annotation { "Feature Type Name" : "Feature", "Feature Type Description" : "" }
export const myFeature = defineFeature(function(context is Context, id is Id, definition is map)
    precondition{}
    {
        {
            var Q0;
            Q0=qCreatedBy(makeId("Front.planeOp"),FACE);
            var sketch = newSketch(context, id + "F0", { "sketchPlane" : qUnion([Q0])});
            skCircle(sketch, "E0", {"center": v(0, 0) * mm, "radius": 38.1 * mm});
            skCircle(sketch, "E1", {"center": v(0, 0) * mm, "radius": 50.8 * mm});
            skLineSegment(sketch, "E2", {"start": v(0, 46.58) * mm, "end": v(0, 31.75) * mm});
            skLineSegment(sketch, "E3", {"start": v(0, 63.5) * mm, "end": v(0, 50.8) * mm});
            skLineSegment(sketch, "E4.1.0", {"start": v(-27.38, 37.68) * mm, "end": v(-18.66, 25.69) * mm});
            skLineSegment(sketch, "E4.2.0", {"start": v(-44.3, 14.4) * mm, "end": v(-30.2, 9.81) * mm});
            skLineSegment(sketch, "E4.3.0", {"start": v(-44.3, -14.4) * mm, "end": v(-30.2, -9.81) * mm});
            skLineSegment(sketch, "E4.4.0", {"start": v(-27.38, -37.68) * mm, "end": v(-18.66, -25.69) * mm});
            skLineSegment(sketch, "E4.6.0", {"start": v(27.38, -37.68) * mm, "end": v(18.66, -25.69) * mm});
            skLineSegment(sketch, "E4.7.0", {"start": v(44.3, -14.4) * mm, "end": v(30.2, -9.81) * mm});
            skLineSegment(sketch, "E4.8.0", {"start": v(44.3, 14.4) * mm, "end": v(30.2, 9.81) * mm});
            skLineSegment(sketch, "E4.9.0", {"start": v(27.38, 37.68) * mm, "end": v(18.66, 25.69) * mm});
            skLineSegment(sketch, "E5.1.0", {"start": v(-28.57, 49.5) * mm, "end": v(-25.4, 44) * mm});
            skLineSegment(sketch, "E5.2.0", {"start": v(-49.5, 28.58) * mm, "end": v(-44, 25.4) * mm});
            skLineSegment(sketch, "E5.3.0", {"start": v(-63.5, 0) * mm, "end": v(-50.8, 0) * mm});
            skLineSegment(sketch, "E5.4.0", {"start": v(-49.5, -28.57) * mm, "end": v(-44, -25.4) * mm});
            skLineSegment(sketch, "E5.5.0", {"start": v(-28.57, -49.5) * mm, "end": v(-25.4, -44) * mm});
            skLineSegment(sketch, "E5.6.0", {"start": v(0, -63.5) * mm, "end": v(0, -50.8) * mm});
            skLineSegment(sketch, "E5.7.0", {"start": v(28.57, -49.5) * mm, "end": v(25.4, -44) * mm});
            skLineSegment(sketch, "E5.8.0", {"start": v(49.5, -28.58) * mm, "end": v(44, -25.4) * mm});
            skLineSegment(sketch, "E5.9.0", {"start": v(63.5, 0) * mm, "end": v(50.8, 0) * mm});
            skLineSegment(sketch, "E5.10.0", {"start": v(49.5, 28.58) * mm, "end": v(44, 25.4) * mm});
            skLineSegment(sketch, "E5.11.0", {"start": v(28.58, 49.5) * mm, "end": v(25.4, 44) * mm});
            skCircle(sketch, "E6.0", {"center": v(0, 0) * mm, "radius": 31.75 * mm});
            skPoint(sketch, "E7.orphan", {"position": v(0, 57.15) * mm});
            skPoint(sketch, "E8.orphan", {"position": v(57.15, 0) * mm});
            skPoint(sketch, "E9.orphan", {"position": v(0, -57.15) * mm});
            skPoint(sketch, "E10.orphan", {"position": v(-57.15, 0) * mm});
            skPoint(sketch, "E11.orphan", {"position": v(0, 38.1) * mm});
            skPoint(sketch, "E12.orphan", {"position": v(22.4, 30.82) * mm});
            skPoint(sketch, "E13.orphan", {"position": v(36.24, 11.77) * mm});
            skPoint(sketch, "E14.orphan", {"position": v(36.24, -11.77) * mm});
            skPoint(sketch, "E15.orphan", {"position": v(22.4, -30.82) * mm});
            skPoint(sketch, "E16.orphan", {"position": v(0, -38.1) * mm});
            skPoint(sketch, "E17.orphan", {"position": v(-22.4, -30.82) * mm});
            skPoint(sketch, "E18.orphan", {"position": v(-36.24, -11.77) * mm});
            skPoint(sketch, "E19.orphan", {"position": v(-36.24, 11.77) * mm});
            skPoint(sketch, "E20.orphan", {"position": v(-22.4, 30.82) * mm});
            skCircle(sketch, "E21.0", {"center": v(0, 0) * mm, "radius": 53.98 * mm});
            skLineSegment(sketch, "E22", {"start": v(0, 50.8) * mm, "end": v(0, 53.98) * mm});
            skLineSegment(sketch, "E23", {"start": v(0, -50.8) * mm, "end": v(0, -53.98) * mm});
            skLineSegment(sketch, "E24.1.0", {"start": v(5.31, -50.52) * mm, "end": v(5.64, -53.68) * mm});
            skLineSegment(sketch, "E24.2.0", {"start": v(10.56, -49.69) * mm, "end": v(11.22, -52.8) * mm});
            skLineSegment(sketch, "E24.3.0", {"start": v(15.7, -48.31) * mm, "end": v(16.68, -51.33) * mm});
            skLineSegment(sketch, "E24.4.0", {"start": v(20.66, -46.4) * mm, "end": v(21.95, -49.3) * mm});
            skLineSegment(sketch, "E24.5.0", {"start": v(25.4, -44) * mm, "end": v(26.99, -46.74) * mm});
            skLineSegment(sketch, "E24.6.0", {"start": v(29.86, -41.1) * mm, "end": v(31.73, -43.67) * mm});
            skLineSegment(sketch, "E24.7.0", {"start": v(34, -37.75) * mm, "end": v(36.12, -40.11) * mm});
            skLineSegment(sketch, "E24.8.0", {"start": v(37.75, -34) * mm, "end": v(40.11, -36.12) * mm});
            skLineSegment(sketch, "E24.9.0", {"start": v(41.1, -29.86) * mm, "end": v(43.67, -31.73) * mm});
            skLineSegment(sketch, "E24.10.0", {"start": v(44, -25.4) * mm, "end": v(46.74, -26.99) * mm});
            skLineSegment(sketch, "E24.11.0", {"start": v(46.4, -20.66) * mm, "end": v(49.3, -21.95) * mm});
            skLineSegment(sketch, "E24.12.0", {"start": v(48.31, -15.7) * mm, "end": v(51.33, -16.68) * mm});
            skLineSegment(sketch, "E24.13.0", {"start": v(49.69, -10.56) * mm, "end": v(52.8, -11.22) * mm});
            skLineSegment(sketch, "E24.14.0", {"start": v(50.52, -5.31) * mm, "end": v(53.68, -5.64) * mm});
            skLineSegment(sketch, "E24.15.0", {"start": v(50.8, 0) * mm, "end": v(53.98, 0) * mm});
            skLineSegment(sketch, "E24.16.0", {"start": v(50.52, 5.31) * mm, "end": v(53.68, 5.64) * mm});
            skLineSegment(sketch, "E24.17.0", {"start": v(49.69, 10.56) * mm, "end": v(52.8, 11.22) * mm});
            skLineSegment(sketch, "E24.18.0", {"start": v(48.31, 15.7) * mm, "end": v(51.33, 16.68) * mm});
            skLineSegment(sketch, "E24.19.0", {"start": v(46.4, 20.66) * mm, "end": v(49.3, 21.95) * mm});
            skLineSegment(sketch, "E24.20.0", {"start": v(44, 25.4) * mm, "end": v(46.74, 26.99) * mm});
            skLineSegment(sketch, "E24.21.0", {"start": v(41.1, 29.86) * mm, "end": v(43.67, 31.73) * mm});
            skLineSegment(sketch, "E24.22.0", {"start": v(37.75, 34) * mm, "end": v(40.11, 36.12) * mm});
            skLineSegment(sketch, "E24.23.0", {"start": v(34, 37.75) * mm, "end": v(36.12, 40.11) * mm});
            skLineSegment(sketch, "E24.24.0", {"start": v(29.86, 41.1) * mm, "end": v(31.73, 43.67) * mm});
            skLineSegment(sketch, "E24.25.0", {"start": v(25.4, 44) * mm, "end": v(26.99, 46.74) * mm});
            skLineSegment(sketch, "E24.26.0", {"start": v(20.66, 46.4) * mm, "end": v(21.95, 49.3) * mm});
            skLineSegment(sketch, "E24.27.0", {"start": v(15.7, 48.31) * mm, "end": v(16.68, 51.33) * mm});
            skLineSegment(sketch, "E24.28.0", {"start": v(10.56, 49.69) * mm, "end": v(11.22, 52.8) * mm});
            skLineSegment(sketch, "E24.29.0", {"start": v(5.31, 50.52) * mm, "end": v(5.64, 53.68) * mm});
            skLineSegment(sketch, "E24.31.0", {"start": v(-5.31, 50.52) * mm, "end": v(-5.64, 53.68) * mm});
            skLineSegment(sketch, "E24.32.0", {"start": v(-10.56, 49.69) * mm, "end": v(-11.22, 52.8) * mm});
            skLineSegment(sketch, "E24.33.0", {"start": v(-15.7, 48.31) * mm, "end": v(-16.68, 51.33) * mm});
            skLineSegment(sketch, "E24.34.0", {"start": v(-20.66, 46.4) * mm, "end": v(-21.95, 49.3) * mm});
            skLineSegment(sketch, "E24.35.0", {"start": v(-25.4, 44) * mm, "end": v(-26.99, 46.74) * mm});
            skLineSegment(sketch, "E24.36.0", {"start": v(-29.86, 41.1) * mm, "end": v(-31.73, 43.67) * mm});
            skLineSegment(sketch, "E24.37.0", {"start": v(-34, 37.75) * mm, "end": v(-36.12, 40.11) * mm});
            skLineSegment(sketch, "E24.38.0", {"start": v(-37.75, 34) * mm, "end": v(-40.11, 36.12) * mm});
            skLineSegment(sketch, "E24.39.0", {"start": v(-41.1, 29.86) * mm, "end": v(-43.67, 31.73) * mm});
            skLineSegment(sketch, "E24.40.0", {"start": v(-44, 25.4) * mm, "end": v(-46.74, 26.99) * mm});
            skLineSegment(sketch, "E24.41.0", {"start": v(-46.4, 20.66) * mm, "end": v(-49.3, 21.95) * mm});
            skLineSegment(sketch, "E24.42.0", {"start": v(-48.31, 15.7) * mm, "end": v(-51.33, 16.68) * mm});
            skLineSegment(sketch, "E24.43.0", {"start": v(-49.69, 10.56) * mm, "end": v(-52.8, 11.22) * mm});
            skLineSegment(sketch, "E24.44.0", {"start": v(-50.52, 5.31) * mm, "end": v(-53.68, 5.64) * mm});
            skLineSegment(sketch, "E24.45.0", {"start": v(-50.8, 0) * mm, "end": v(-53.98, 0) * mm});
            skLineSegment(sketch, "E24.46.0", {"start": v(-50.52, -5.31) * mm, "end": v(-53.68, -5.64) * mm});
            skLineSegment(sketch, "E24.47.0", {"start": v(-49.69, -10.56) * mm, "end": v(-52.8, -11.22) * mm});
            skLineSegment(sketch, "E24.48.0", {"start": v(-48.31, -15.7) * mm, "end": v(-51.33, -16.68) * mm});
            skLineSegment(sketch, "E24.49.0", {"start": v(-46.4, -20.66) * mm, "end": v(-49.3, -21.95) * mm});
            skLineSegment(sketch, "E24.50.0", {"start": v(-44, -25.4) * mm, "end": v(-46.74, -26.99) * mm});
            skLineSegment(sketch, "E24.51.0", {"start": v(-41.1, -29.86) * mm, "end": v(-43.67, -31.73) * mm});
            skLineSegment(sketch, "E24.52.0", {"start": v(-37.75, -34) * mm, "end": v(-40.11, -36.12) * mm});
            skLineSegment(sketch, "E24.53.0", {"start": v(-34, -37.75) * mm, "end": v(-36.12, -40.11) * mm});
            skLineSegment(sketch, "E24.54.0", {"start": v(-29.86, -41.1) * mm, "end": v(-31.73, -43.67) * mm});
            skLineSegment(sketch, "E24.55.0", {"start": v(-25.4, -44) * mm, "end": v(-26.99, -46.74) * mm});
            skLineSegment(sketch, "E24.56.0", {"start": v(-20.66, -46.4) * mm, "end": v(-21.95, -49.3) * mm});
            skLineSegment(sketch, "E24.57.0", {"start": v(-15.7, -48.31) * mm, "end": v(-16.68, -51.33) * mm});
            skLineSegment(sketch, "E24.58.0", {"start": v(-10.56, -49.69) * mm, "end": v(-11.22, -52.8) * mm});
            skLineSegment(sketch, "E24.59.0", {"start": v(-5.31, -50.52) * mm, "end": v(-5.64, -53.68) * mm});
            skLineSegment(sketch, "E25", {"start": v(0, -31.75) * mm, "end": v(0, -38.1) * mm});
            skLineSegment(sketch, "E26.1.0", {"start": v(2, -31.69) * mm, "end": v(2.4, -38.02) * mm});
            skLineSegment(sketch, "E26.2.0", {"start": v(3.98, -31.5) * mm, "end": v(4.78, -37.8) * mm});
            skLineSegment(sketch, "E26.3.0", {"start": v(5.95, -31.19) * mm, "end": v(7.14, -37.43) * mm});
            skLineSegment(sketch, "E26.4.0", {"start": v(7.9, -30.75) * mm, "end": v(9.48, -36.9) * mm});
            skLineSegment(sketch, "E26.5.0", {"start": v(9.81, -30.2) * mm, "end": v(11.77, -36.24) * mm});
            skLineSegment(sketch, "E26.6.0", {"start": v(11.69, -29.52) * mm, "end": v(14.03, -35.42) * mm});
            skLineSegment(sketch, "E26.7.0", {"start": v(13.52, -28.73) * mm, "end": v(16.22, -34.47) * mm});
            skLineSegment(sketch, "E26.8.0", {"start": v(15.3, -27.82) * mm, "end": v(18.35, -33.39) * mm});
            skLineSegment(sketch, "E26.9.0", {"start": v(17.01, -26.8) * mm, "end": v(20.41, -32.17) * mm});
            skLineSegment(sketch, "E26.10.0", {"start": v(18.66, -25.69) * mm, "end": v(22.4, -30.82) * mm});
            skLineSegment(sketch, "E26.11.0", {"start": v(20.24, -24.46) * mm, "end": v(24.29, -29.36) * mm});
            skLineSegment(sketch, "E26.12.0", {"start": v(21.73, -23.14) * mm, "end": v(26.08, -27.77) * mm});
            skLineSegment(sketch, "E26.13.0", {"start": v(23.14, -21.73) * mm, "end": v(27.77, -26.08) * mm});
            skLineSegment(sketch, "E26.14.0", {"start": v(24.46, -20.24) * mm, "end": v(29.36, -24.29) * mm});
            skLineSegment(sketch, "E26.15.0", {"start": v(25.69, -18.66) * mm, "end": v(30.82, -22.4) * mm});
            skLineSegment(sketch, "E26.16.0", {"start": v(26.8, -17.01) * mm, "end": v(32.17, -20.42) * mm});
            skLineSegment(sketch, "E26.17.0", {"start": v(27.82, -15.3) * mm, "end": v(33.39, -18.35) * mm});
            skLineSegment(sketch, "E26.18.0", {"start": v(28.73, -13.52) * mm, "end": v(34.47, -16.22) * mm});
            skLineSegment(sketch, "E26.19.0", {"start": v(29.52, -11.69) * mm, "end": v(35.42, -14.03) * mm});
            skLineSegment(sketch, "E26.20.0", {"start": v(30.2, -9.81) * mm, "end": v(36.24, -11.77) * mm});
            skLineSegment(sketch, "E26.21.0", {"start": v(30.75, -7.9) * mm, "end": v(36.9, -9.48) * mm});
            skLineSegment(sketch, "E26.22.0", {"start": v(31.19, -5.95) * mm, "end": v(37.43, -7.14) * mm});
            skLineSegment(sketch, "E26.23.0", {"start": v(31.5, -3.98) * mm, "end": v(37.8, -4.78) * mm});
            skLineSegment(sketch, "E26.24.0", {"start": v(31.69, -2) * mm, "end": v(38.02, -2.4) * mm});
            skLineSegment(sketch, "E26.25.0", {"start": v(31.75, 0) * mm, "end": v(38.1, 0) * mm});
            skLineSegment(sketch, "E26.26.0", {"start": v(31.69, 2) * mm, "end": v(38.02, 2.4) * mm});
            skLineSegment(sketch, "E26.27.0", {"start": v(31.5, 3.98) * mm, "end": v(37.8, 4.78) * mm});
            skLineSegment(sketch, "E26.28.0", {"start": v(31.19, 5.95) * mm, "end": v(37.43, 7.14) * mm});
            skLineSegment(sketch, "E26.29.0", {"start": v(30.75, 7.9) * mm, "end": v(36.9, 9.48) * mm});
            skLineSegment(sketch, "E26.30.0", {"start": v(30.2, 9.81) * mm, "end": v(36.24, 11.77) * mm});
            skLineSegment(sketch, "E26.31.0", {"start": v(29.52, 11.69) * mm, "end": v(35.42, 14.03) * mm});
            skLineSegment(sketch, "E26.32.0", {"start": v(28.73, 13.52) * mm, "end": v(34.47, 16.22) * mm});
            skLineSegment(sketch, "E26.33.0", {"start": v(27.82, 15.3) * mm, "end": v(33.39, 18.35) * mm});
            skLineSegment(sketch, "E26.34.0", {"start": v(26.8, 17.01) * mm, "end": v(32.17, 20.41) * mm});
            skLineSegment(sketch, "E26.35.0", {"start": v(25.69, 18.66) * mm, "end": v(30.82, 22.4) * mm});
            skLineSegment(sketch, "E26.36.0", {"start": v(24.46, 20.24) * mm, "end": v(29.36, 24.29) * mm});
            skLineSegment(sketch, "E26.37.0", {"start": v(23.14, 21.73) * mm, "end": v(27.77, 26.08) * mm});
            skLineSegment(sketch, "E26.38.0", {"start": v(21.73, 23.14) * mm, "end": v(26.08, 27.77) * mm});
            skLineSegment(sketch, "E26.39.0", {"start": v(20.24, 24.46) * mm, "end": v(24.29, 29.36) * mm});
            skLineSegment(sketch, "E26.40.0", {"start": v(18.66, 25.69) * mm, "end": v(22.4, 30.82) * mm});
            skLineSegment(sketch, "E26.41.0", {"start": v(17.01, 26.8) * mm, "end": v(20.42, 32.17) * mm});
            skLineSegment(sketch, "E26.42.0", {"start": v(15.3, 27.82) * mm, "end": v(18.35, 33.39) * mm});
            skLineSegment(sketch, "E26.43.0", {"start": v(13.52, 28.73) * mm, "end": v(16.22, 34.47) * mm});
            skLineSegment(sketch, "E26.44.0", {"start": v(11.69, 29.52) * mm, "end": v(14.03, 35.42) * mm});
            skLineSegment(sketch, "E26.45.0", {"start": v(9.81, 30.2) * mm, "end": v(11.77, 36.24) * mm});
            skLineSegment(sketch, "E26.46.0", {"start": v(7.9, 30.75) * mm, "end": v(9.48, 36.9) * mm});
            skLineSegment(sketch, "E26.47.0", {"start": v(5.95, 31.19) * mm, "end": v(7.14, 37.43) * mm});
            skLineSegment(sketch, "E26.48.0", {"start": v(3.98, 31.5) * mm, "end": v(4.78, 37.8) * mm});
            skLineSegment(sketch, "E26.49.0", {"start": v(2, 31.69) * mm, "end": v(2.4, 38.02) * mm});
            skLineSegment(sketch, "E26.50.0", {"start": v(0, 31.75) * mm, "end": v(0, 38.1) * mm});
            skLineSegment(sketch, "E26.51.0", {"start": v(-2, 31.69) * mm, "end": v(-2.4, 38.02) * mm});
            skLineSegment(sketch, "E26.52.0", {"start": v(-3.98, 31.5) * mm, "end": v(-4.78, 37.8) * mm});
            skLineSegment(sketch, "E26.53.0", {"start": v(-5.95, 31.19) * mm, "end": v(-7.14, 37.43) * mm});
            skLineSegment(sketch, "E26.54.0", {"start": v(-7.9, 30.75) * mm, "end": v(-9.48, 36.9) * mm});
            skLineSegment(sketch, "E26.55.0", {"start": v(-9.81, 30.2) * mm, "end": v(-11.77, 36.24) * mm});
            skLineSegment(sketch, "E26.56.0", {"start": v(-11.69, 29.52) * mm, "end": v(-14.03, 35.42) * mm});
            skLineSegment(sketch, "E26.57.0", {"start": v(-13.52, 28.73) * mm, "end": v(-16.22, 34.47) * mm});
            skLineSegment(sketch, "E26.58.0", {"start": v(-15.3, 27.82) * mm, "end": v(-18.35, 33.39) * mm});
            skLineSegment(sketch, "E26.59.0", {"start": v(-17.01, 26.8) * mm, "end": v(-20.41, 32.17) * mm});
            skLineSegment(sketch, "E26.60.0", {"start": v(-18.66, 25.69) * mm, "end": v(-22.4, 30.82) * mm});
            skLineSegment(sketch, "E26.61.0", {"start": v(-20.24, 24.46) * mm, "end": v(-24.29, 29.36) * mm});
            skLineSegment(sketch, "E26.62.0", {"start": v(-21.73, 23.14) * mm, "end": v(-26.08, 27.77) * mm});
            skLineSegment(sketch, "E26.63.0", {"start": v(-23.14, 21.73) * mm, "end": v(-27.77, 26.08) * mm});
            skLineSegment(sketch, "E26.64.0", {"start": v(-24.46, 20.24) * mm, "end": v(-29.36, 24.29) * mm});
            skLineSegment(sketch, "E26.65.0", {"start": v(-25.69, 18.66) * mm, "end": v(-30.82, 22.4) * mm});
            skLineSegment(sketch, "E26.66.0", {"start": v(-26.8, 17.01) * mm, "end": v(-32.17, 20.42) * mm});
            skLineSegment(sketch, "E26.67.0", {"start": v(-27.82, 15.3) * mm, "end": v(-33.39, 18.35) * mm});
            skLineSegment(sketch, "E26.68.0", {"start": v(-28.73, 13.52) * mm, "end": v(-34.47, 16.22) * mm});
            skLineSegment(sketch, "E26.69.0", {"start": v(-29.52, 11.69) * mm, "end": v(-35.42, 14.03) * mm});
            skLineSegment(sketch, "E26.70.0", {"start": v(-30.2, 9.81) * mm, "end": v(-36.24, 11.77) * mm});
            skLineSegment(sketch, "E26.71.0", {"start": v(-30.75, 7.9) * mm, "end": v(-36.9, 9.48) * mm});
            skLineSegment(sketch, "E26.72.0", {"start": v(-31.19, 5.95) * mm, "end": v(-37.43, 7.14) * mm});
            skLineSegment(sketch, "E26.73.0", {"start": v(-31.5, 3.98) * mm, "end": v(-37.8, 4.78) * mm});
            skLineSegment(sketch, "E26.74.0", {"start": v(-31.69, 2) * mm, "end": v(-38.02, 2.4) * mm});
            skLineSegment(sketch, "E26.75.0", {"start": v(-31.75, 0) * mm, "end": v(-38.1, 0) * mm});
            skLineSegment(sketch, "E26.76.0", {"start": v(-31.69, -2) * mm, "end": v(-38.02, -2.4) * mm});
            skLineSegment(sketch, "E26.77.0", {"start": v(-31.5, -3.98) * mm, "end": v(-37.8, -4.78) * mm});
            skLineSegment(sketch, "E26.78.0", {"start": v(-31.19, -5.95) * mm, "end": v(-37.43, -7.14) * mm});
            skLineSegment(sketch, "E26.79.0", {"start": v(-30.75, -7.9) * mm, "end": v(-36.9, -9.48) * mm});
            skLineSegment(sketch, "E26.80.0", {"start": v(-30.2, -9.81) * mm, "end": v(-36.24, -11.77) * mm});
            skLineSegment(sketch, "E26.81.0", {"start": v(-29.52, -11.69) * mm, "end": v(-35.42, -14.03) * mm});
            skLineSegment(sketch, "E26.82.0", {"start": v(-28.73, -13.52) * mm, "end": v(-34.47, -16.22) * mm});
            skLineSegment(sketch, "E26.83.0", {"start": v(-27.82, -15.3) * mm, "end": v(-33.39, -18.35) * mm});
            skLineSegment(sketch, "E26.84.0", {"start": v(-26.8, -17.01) * mm, "end": v(-32.17, -20.41) * mm});
            skLineSegment(sketch, "E26.85.0", {"start": v(-25.69, -18.66) * mm, "end": v(-30.82, -22.4) * mm});
            skLineSegment(sketch, "E26.86.0", {"start": v(-24.46, -20.24) * mm, "end": v(-29.36, -24.29) * mm});
            skLineSegment(sketch, "E26.87.0", {"start": v(-23.14, -21.73) * mm, "end": v(-27.77, -26.08) * mm});
            skLineSegment(sketch, "E26.88.0", {"start": v(-21.73, -23.14) * mm, "end": v(-26.08, -27.77) * mm});
            skLineSegment(sketch, "E26.89.0", {"start": v(-20.24, -24.46) * mm, "end": v(-24.29, -29.36) * mm});
            skLineSegment(sketch, "E26.90.0", {"start": v(-18.66, -25.69) * mm, "end": v(-22.4, -30.82) * mm});
            skLineSegment(sketch, "E26.91.0", {"start": v(-17.01, -26.8) * mm, "end": v(-20.42, -32.17) * mm});
            skLineSegment(sketch, "E26.92.0", {"start": v(-15.3, -27.82) * mm, "end": v(-18.35, -33.39) * mm});
            skLineSegment(sketch, "E26.93.0", {"start": v(-13.52, -28.73) * mm, "end": v(-16.22, -34.47) * mm});
            skLineSegment(sketch, "E26.94.0", {"start": v(-11.69, -29.52) * mm, "end": v(-14.03, -35.42) * mm});
            skLineSegment(sketch, "E26.95.0", {"start": v(-9.81, -30.2) * mm, "end": v(-11.77, -36.24) * mm});
            skLineSegment(sketch, "E26.96.0", {"start": v(-7.9, -30.75) * mm, "end": v(-9.48, -36.9) * mm});
            skLineSegment(sketch, "E26.97.0", {"start": v(-5.95, -31.19) * mm, "end": v(-7.14, -37.43) * mm});
            skLineSegment(sketch, "E26.98.0", {"start": v(-3.98, -31.5) * mm, "end": v(-4.78, -37.8) * mm});
            skLineSegment(sketch, "E26.99.0", {"start": v(-2, -31.69) * mm, "end": v(-2.4, -38.02) * mm});
            skLineSegment(sketch, "E27", {"start": v(0, -31.75) * mm, "end": v(0, -44.45) * mm});
            skText(sketch, "E28", { "text": "Decimal Conversion Clock", "fontName": "AllertaStencil-Regular.ttf"});
            skText(sketch, "E29", { "text": "0.0", "fontName": "OpenSans-Regular.ttf"});
            skText(sketch, "E30", { "text": ".1", "fontName": "OpenSans-Regular.ttf"});
            skText(sketch, "E31", { "text": ".2", "fontName": "OpenSans-Regular.ttf"});
            skText(sketch, "E32", { "text": ".3", "fontName": "OpenSans-Regular.ttf"});
            skText(sketch, "E33", { "text": ".4", "fontName": "OpenSans-Regular.ttf"});
            skText(sketch, "E34", { "text": ".5", "fontName": "OpenSans-Regular.ttf"});
            skText(sketch, "E35", { "text": ".6", "fontName": "OpenSans-Regular.ttf"});
            skText(sketch, "E36", { "text": ".7", "fontName": "OpenSans-Regular.ttf"});
            skText(sketch, "E37", { "text": ".8", "fontName": "OpenSans-Regular.ttf"});
            skText(sketch, "E38", { "text": ".9", "fontName": "OpenSans-Regular.ttf"});
            skText(sketch, "E39", { "text": "1.0", "fontName": "OpenSans-Regular.ttf"});
            skText(sketch, "E40", { "text": "12", "fontName": "OpenSans-Regular.ttf"});
            skText(sketch, "E41", { "text": "3\n", "fontName": "OpenSans-Regular.ttf"});
            skText(sketch, "E42", { "text": "6", "fontName": "OpenSans-Regular.ttf"});
            skText(sketch, "E43", { "text": "9", "fontName": "OpenSans-Regular.ttf"});
            const initialGuessF0  = {"E28": [-0.0291, 0, 1, 0, 0.00317], "E29": [0, 0.04658, 1, 0, 0.0019], "E30": [0.02738, 0.03578, 1, 0, 0.0019], "E31": [0.0443, 0.01249, 1, 0, 0.0019], "E32": [0.0443, -0.0163, 1, 0, 0.0019], "E33": [0.02738, -0.03959, 1, 0, 0.0019], "E34": [-0.00112, -0.04635, 1, 0, 0.0019], "E35": [-0.02964, -0.03959, 1, 0, 0.0019], "E36": [-0.04655, -0.0163, 1, 0, 0.0019], "E37": [-0.04655, 0.01249, 1, 0, 0.0019], "E38": [-0.02962, 0.03578, 1, 0, 0.0019], "E39": [-0.00377, 0.04467, 1, 0, 0.0019], "E40": [-0.0051, 0.0635, 1, 0, 0.00635], "E41": [0.06353, -0.00316, 1, 0, 0.00635], "E42": [-0.0026, -0.06985, 1, 0, 0.00635], "E43": [-0.06863, -0.00322, 1, 0, 0.00635]};
            skSetInitialGuess(sketch, initialGuessF0);
            skSolve(sketch);
        }
        {
            var Q0;
            Q0=makeQuery(id+"F0.imprint","IMPRINT",FACE,{"disambiguationData":[TD([[makeQuery(id+"F0.imprint","IMPRINT",EDGE,{"derivedFrom":sQuery(id+"F0.wireOp",EDGE,"E28.sketch_text.stroke-0")}),1.0]])]});
            extrude(context, id + "F1", {"entities" : qUnion([Q0]), "depth" : 3.17 * mm, "offsetDistance" : 25.4 * mm});
        }
    });